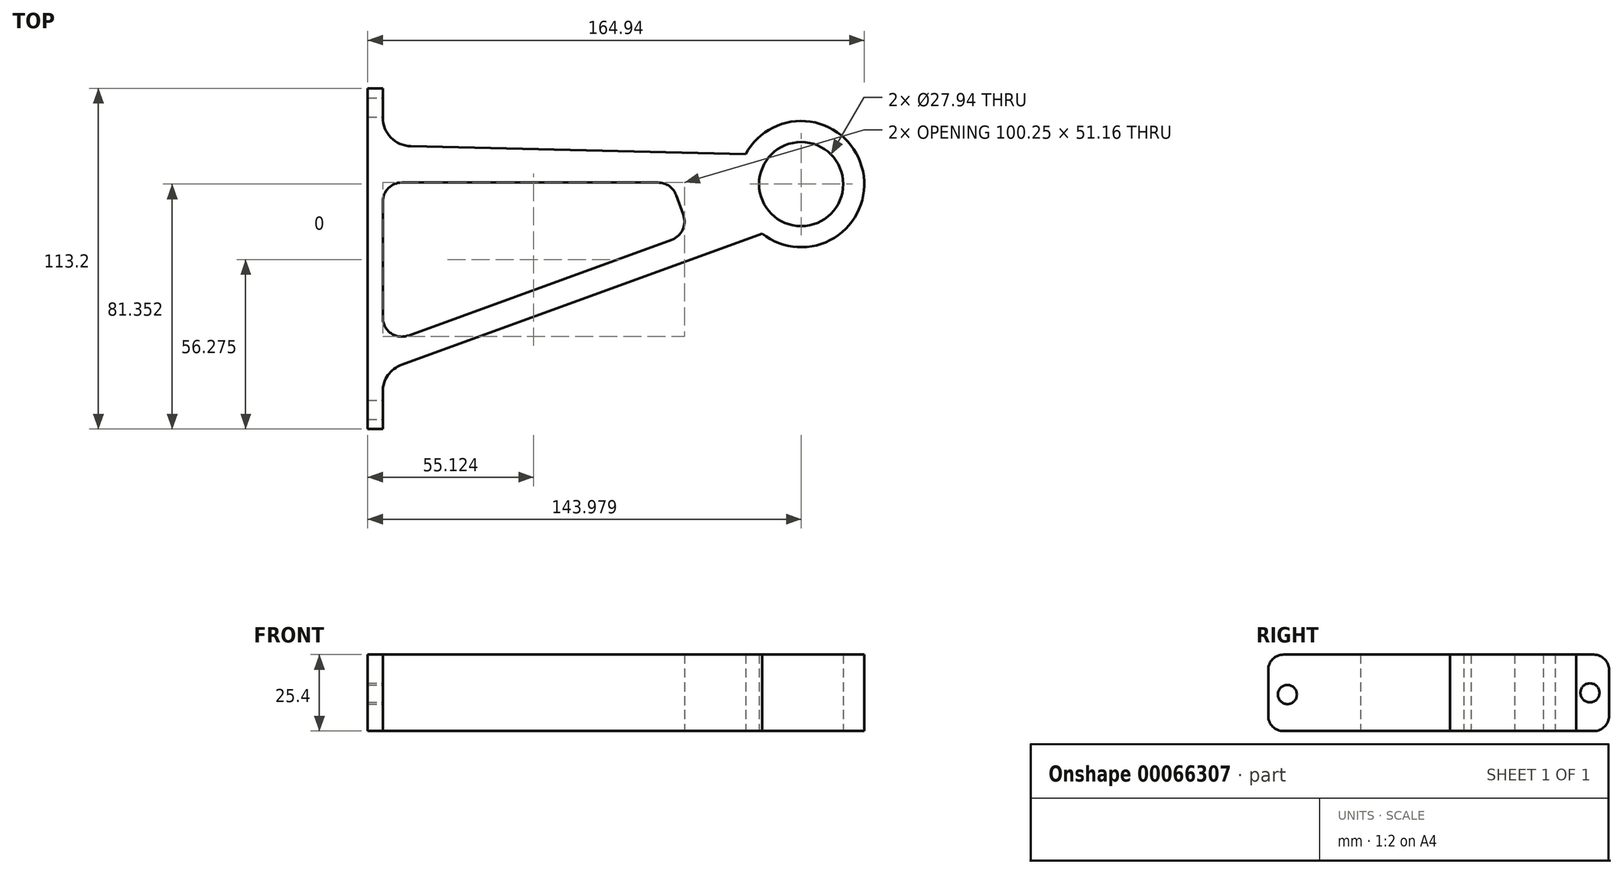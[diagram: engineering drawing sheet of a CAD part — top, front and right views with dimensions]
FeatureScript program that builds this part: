
annotation { "Feature Type Name" : "Feature", "Feature Type Description" : "" }
export const myFeature = defineFeature(function(context is Context, id is Id, definition is map)
    precondition{}
    {
        {
            var Q0;
            Q0=qCreatedBy(makeId("Top.planeOp"),FACE);
            var sketch = newSketch(context, id + "F0", { "sketchPlane" : qUnion([Q0])});
            skLineSegment(sketch, "E0.bottom", {"start": v(-132, 52.26) * mm, "end": v(-127, 52.26) * mm});
            skLineSegment(sketch, "E0.top", {"start": v(-132, -60.94) * mm, "end": v(-127, -60.94) * mm});
            skLineSegment(sketch, "E0.left", {"start": v(-132, 52.26) * mm, "end": v(-132, -60.94) * mm});
            skLineSegment(sketch, "E0.right", {"start": v(-127, 14.56) * mm, "end": v(-127, -23.93) * mm});
            skLineSegment(sketch, "E1", {"start": v(-127, -41.9) * mm, "end": v(-1.01, 3.97) * mm});
            skLineSegment(sketch, "E2", {"start": v(-118.48, -29.9) * mm, "end": v(-30.92, 1.97) * mm});
            skLineSegment(sketch, "E3", {"start": v(-127, 33.21) * mm, "end": v(-6.45, 30.4) * mm});
            skLineSegment(sketch, "E4", {"start": v(-120.65, 20.91) * mm, "end": v(-35.5, 20.91) * mm});
            skLineSegment(sketch, "E5", {"start": v(-29.54, 16.73) * mm, "end": v(-27.13, 10.1) * mm});
            skArc(sketch, "E6.filletArc", {"start": v(-29.54, 16.73) * mm, "mid": v(-31.87, 19.76) * mm, "end": v(-35.5, 20.91) * mm});
            skArc(sketch, "E7.filletArc", {"start": v(-30.92, 1.97) * mm, "mid": v(-27.34, 5.25) * mm, "end": v(-27.13, 10.1) * mm});
            skArc(sketch, "E8.filletArc", {"start": v(-120.65, 20.91) * mm, "mid": v(-125.14, 19.05) * mm, "end": v(-127, 14.56) * mm});
            skArc(sketch, "E9.filletArc", {"start": v(-127, -23.93) * mm, "mid": v(-124.3, -29.13) * mm, "end": v(-118.48, -29.9) * mm});
            skLineSegment(sketch, "E10", {"start": v(-127, 52.26) * mm, "end": v(-127, 33.21) * mm});
            skArc(sketch, "E11", {"start": v(-1.01, 3.97) * mm, "mid": v(32.5, 24.64) * mm, "end": v(-6.45, 30.4) * mm});
            skLineSegment(sketch, "E12", {"start": v(-127, -41.9) * mm, "end": v(-127, -60.94) * mm});
            skCircle(sketch, "E13", {"center": v(11.98, 20.41) * mm, "radius": 13.97 * mm});
            skSolve(sketch);
        }
        {
            var Q0;
            Q0 = qSketchRegion(id + "F0", true);
            extrude(context, id + "F1", {"entities" : qUnion([Q0]), "depth" : 25.4 * mm});
        }
        {
            var Q0;
            Q0=makeQuery(id+"F1.opExtrude","CAP_EDGE",EDGE,{"disambiguationData":[OSD([sQuery(id+"F0.wireOp",EDGE,"E0.bottom")])],"isStart":false});
            var Q1;
            Q1=makeQuery(id+"F1.opExtrude","CAP_EDGE",EDGE,{"disambiguationData":[OSD([sQuery(id+"F0.wireOp",EDGE,"E0.bottom")])],"isStart":true});
            var Q2;
            Q2=makeQuery(id+"F1.opExtrude","CAP_EDGE",EDGE,{"disambiguationData":[OSD([sQuery(id+"F0.wireOp",EDGE,"E0.top")])],"isStart":true});
            var Q3;
            Q3=makeQuery(id+"F1.opExtrude","CAP_EDGE",EDGE,{"disambiguationData":[OSD([sQuery(id+"F0.wireOp",EDGE,"E0.top")])],"isStart":false});
            fillet(context, id + "F2", {"entities" : qUnion([Q0, Q1, Q2, Q3]), "radius" : 5.08 * mm, "tangentPropagation" : true, "allowEdgeOverflow" : false});
        }
        {
            var Q0;
            Q0=makeQuery(id+"F1.opExtrude","SWEPT_FACE",FACE,{"disambiguationData":[OSD([sQuery(id+"F0.wireOp",EDGE,"E12")])]});
            var sketch = newSketch(context, id + "F3", { "sketchPlane" : qUnion([Q0])});
            skCircle(sketch, "E14", {"center": v(45.91, 12.7) * mm, "radius": 3.18 * mm});
            skCircle(sketch, "E15", {"center": v(-54.6, 12.16) * mm, "radius": 3.18 * mm});
            skSolve(sketch);
        }
        {
            var Q0;
            Q0 = qSketchRegion(id + "F3", true);
            extrude(context, id + "F4", {"entities" : qUnion([Q0]), "operationType" : NewBodyOperationType.REMOVE, "endBound" : BoundingType.THROUGH_ALL, "oppositeDirection" : true, "depth" : 25.4 * mm});
        }
        {
            var Q0;
            Q0=makeQuery(id+"F1.opExtrude","SWEPT_EDGE",EDGE,{"disambiguationData":[OSD([sQuery(id+"F0.wireOp",EDGE,"E1"),sQuery(id+"F0.wireOp",EDGE,"E12")])]});
            var Q1;
            Q1=makeQuery(id+"F1.opExtrude","SWEPT_EDGE",EDGE,{"disambiguationData":[OSD([sQuery(id+"F0.wireOp",EDGE,"E3"),sQuery(id+"F0.wireOp",EDGE,"E10")])]});
            fillet(context, id + "F5", {"entities" : qUnion([Q0, Q1]), "radius" : 9.57 * mm, "tangentPropagation" : true, "allowEdgeOverflow" : false});
        }
    });
